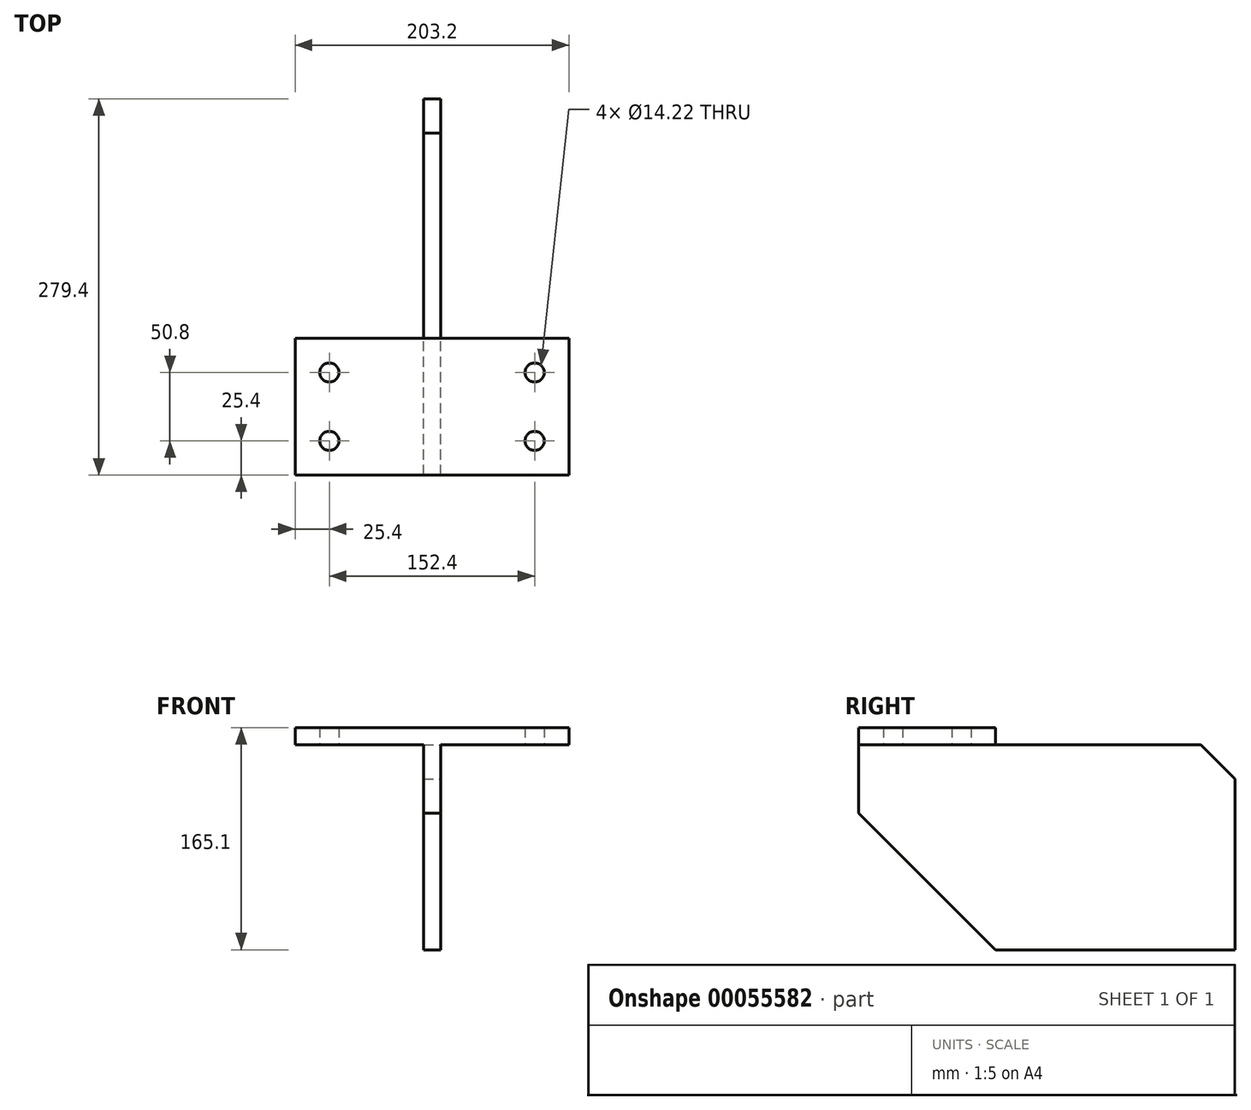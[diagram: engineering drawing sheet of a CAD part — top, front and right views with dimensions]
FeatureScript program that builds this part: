
annotation { "Feature Type Name" : "Feature", "Feature Type Description" : "" }
export const myFeature = defineFeature(function(context is Context, id is Id, definition is map)
    precondition{}
    {
        {
            var Q0;
            Q0=qCreatedBy(makeId("Top.planeOp"),FACE);
            var sketch = newSketch(context, id + "F0", { "sketchPlane" : qUnion([Q0])});
            skLineSegment(sketch, "E0.0", {"start": v(-101.6, 50.8) * mm, "end": v(-101.6, -50.8) * mm});
            skLineSegment(sketch, "E1.0", {"start": v(-101.6, -50.8) * mm, "end": v(101.6, -50.8) * mm});
            skCircle(sketch, "E2.0", {"center": v(-76.2, -25.4) * mm, "radius": 7.11 * mm});
            skCircle(sketch, "E3.0", {"center": v(-76.2, 25.4) * mm, "radius": 7.11 * mm});
            skLineSegment(sketch, "E4.0", {"start": v(-101.6, 50.8) * mm, "end": v(101.6, 50.8) * mm});
            skCircle(sketch, "E5.0", {"center": v(76.2, 25.4) * mm, "radius": 7.11 * mm});
            skCircle(sketch, "E6.0", {"center": v(76.2, -25.4) * mm, "radius": 7.11 * mm});
            skLineSegment(sketch, "E7.0", {"start": v(101.6, 50.8) * mm, "end": v(101.6, -50.8) * mm});
            skSolve(sketch);
        }
        {
            var Q0;
            Q0=qSketchRegion(id+"F0",true);
            extrude(context, id + "F1", {"entities" : qUnion([Q0]), "depth" : 12.7 * mm});
        }
        {
            var Q0;
            Q0=makeQuery(id+"F1.opExtrude","CAP_FACE",FACE,{"disambiguationData":[OSD([sQuery(id+"F0.wireOp",EDGE,"E0.0"),sQuery(id+"F0.wireOp",EDGE,"E1.0"),sQuery(id+"F0.wireOp",EDGE,"E2.0"),sQuery(id+"F0.wireOp",EDGE,"E3.0"),sQuery(id+"F0.wireOp",EDGE,"E4.0"),sQuery(id+"F0.wireOp",EDGE,"E5.0"),sQuery(id+"F0.wireOp",EDGE,"E6.0"),sQuery(id+"F0.wireOp",EDGE,"E7.0")])],"isStart":true});
            var sketch = newSketch(context, id + "F2", { "sketchPlane" : qUnion([Q0])});
            skLineSegment(sketch, "E8.0", {"start": v(-101.6, 50.8) * mm, "end": v(101.6, 50.8) * mm, "construction": true});
            skLineSegment(sketch, "E9", {"start": v(0, 0) * mm, "end": v(0, 111.66) * mm, "construction": true});
            skPoint(sketch, "E9.endSnap0", {"position": v(0, 50.8) * mm});
            skLineSegment(sketch, "E10.0", {"start": v(-6.35, 0) * mm, "end": v(-6.35, 111.66) * mm, "construction": true});
            skLineSegment(sketch, "E11.bottom", {"start": v(-6.35, 50.8) * mm, "end": v(6.35, 50.8) * mm});
            skLineSegment(sketch, "E11.top", {"start": v(-6.35, -228.6) * mm, "end": v(6.35, -228.6) * mm});
            skLineSegment(sketch, "E11.left", {"start": v(-6.35, 50.8) * mm, "end": v(-6.35, -228.6) * mm});
            skLineSegment(sketch, "E11.right", {"start": v(6.35, 50.8) * mm, "end": v(6.35, -228.6) * mm});
            skSolve(sketch);
        }
        {
            var Q0;
            Q0=qSketchRegion(id+"F2",true);
            extrude(context, id + "F3", {"entities" : qUnion([Q0]), "operationType" : NewBodyOperationType.ADD, "depth" : 152.4 * mm});
        }
        {
            var Q0;
            Q0=makeQuery(id+"F3.opExtrude","CAP_EDGE",EDGE,{"disambiguationData":[OSD([sQuery(id+"F2.wireOp",EDGE,"E11.bottom")])],"isStart":false});
            chamfer(context, id + "F4", {"entities" : qUnion([Q0]), "width" : 101.6 * mm, "tangentPropagation" : true});
        }
        {
            var Q0;
            Q0=makeQuery(id+"F3.opExtrude","CAP_EDGE",EDGE,{"disambiguationData":[OSD([sQuery(id+"F2.wireOp",EDGE,"E11.top")])],"isStart":true});
            chamfer(context, id + "F5", {"entities" : qUnion([Q0]), "width" : 25.4 * mm, "tangentPropagation" : true});
        }
    });
